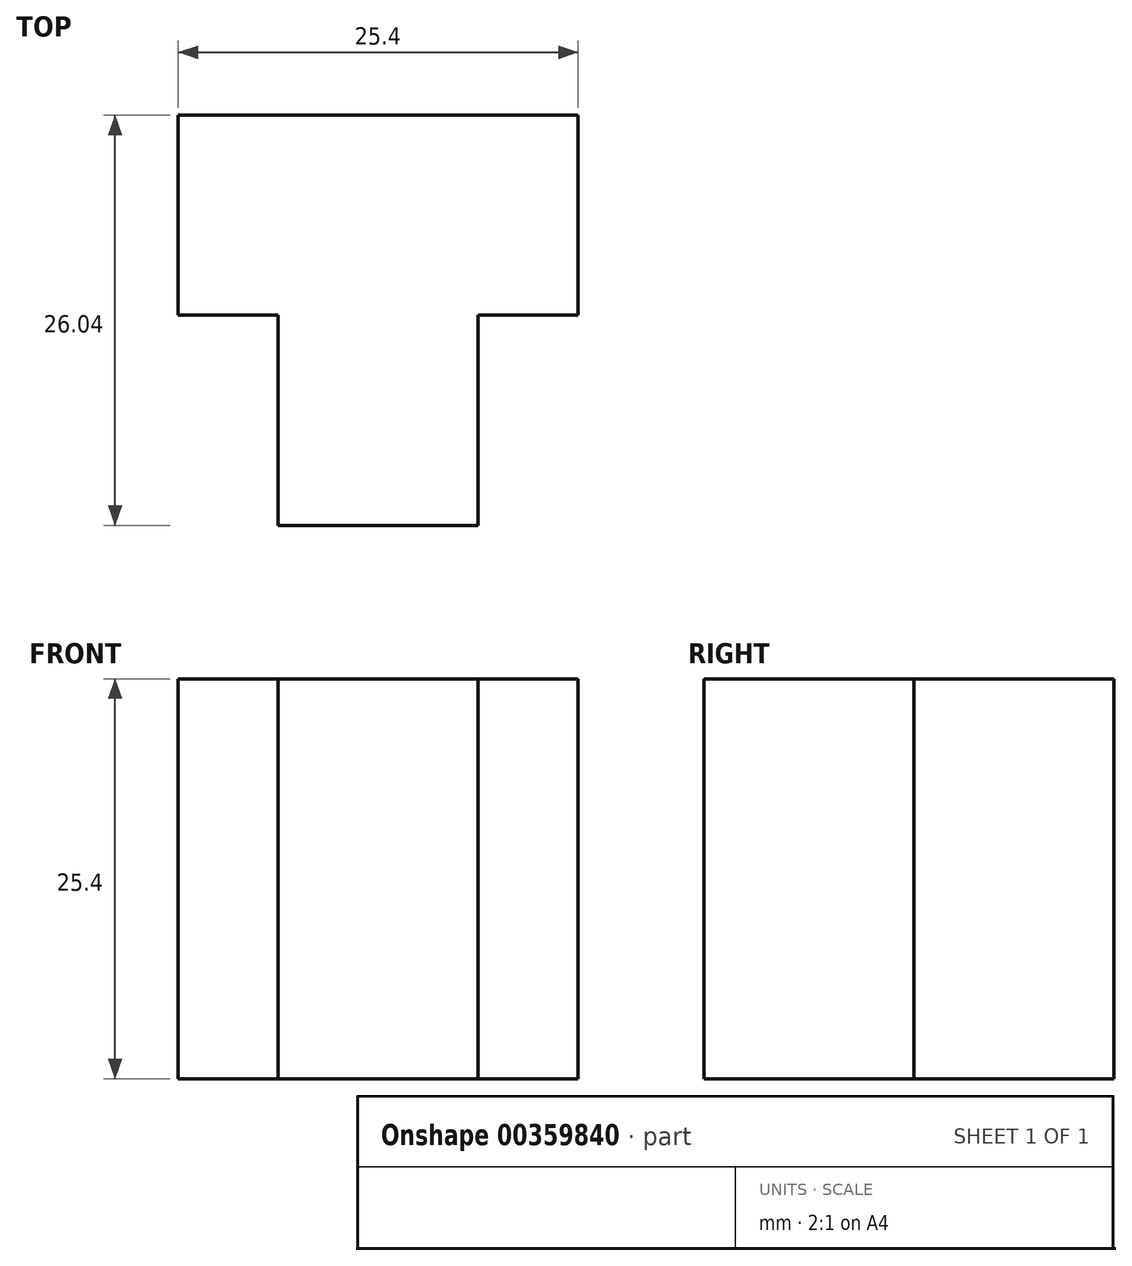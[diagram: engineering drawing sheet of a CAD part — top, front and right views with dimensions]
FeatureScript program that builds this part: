
annotation { "Feature Type Name" : "Feature", "Feature Type Description" : "" }
export const myFeature = defineFeature(function(context is Context, id is Id, definition is map)
    precondition{}
    {
        {
            var Q0;
            Q0=qCreatedBy(makeId("Top.planeOp"),FACE);
            var sketch = newSketch(context, id + "F0", { "sketchPlane" : qUnion([Q0])});
            skLineSegment(sketch, "E0", {"start": v(-25.08, -1.96) * mm, "end": v(-25.08, 11.38) * mm});
            skLineSegment(sketch, "E1", {"start": v(-25.08, 11.38) * mm, "end": v(-31.43, 11.38) * mm});
            skLineSegment(sketch, "E2", {"start": v(-31.43, 11.38) * mm, "end": v(-31.43, 24.08) * mm});
            skLineSegment(sketch, "E3", {"start": v(-31.43, 24.08) * mm, "end": v(-6.03, 24.08) * mm});
            skLineSegment(sketch, "E4", {"start": v(-6.03, 24.08) * mm, "end": v(-6.03, 11.38) * mm});
            skLineSegment(sketch, "E5", {"start": v(-6.03, 11.38) * mm, "end": v(-12.38, 11.38) * mm});
            skLineSegment(sketch, "E6", {"start": v(-12.38, 11.38) * mm, "end": v(-12.38, -1.96) * mm});
            skLineSegment(sketch, "E7", {"start": v(-12.38, -1.96) * mm, "end": v(-25.08, -1.96) * mm});
            skSolve(sketch);
        }
        {
            var Q0;
            Q0 = qSketchRegion(id + "F0", true);
            extrude(context, id + "F1", {"entities" : qUnion([Q0]), "depth" : 25.4 * mm});
        }
    });
